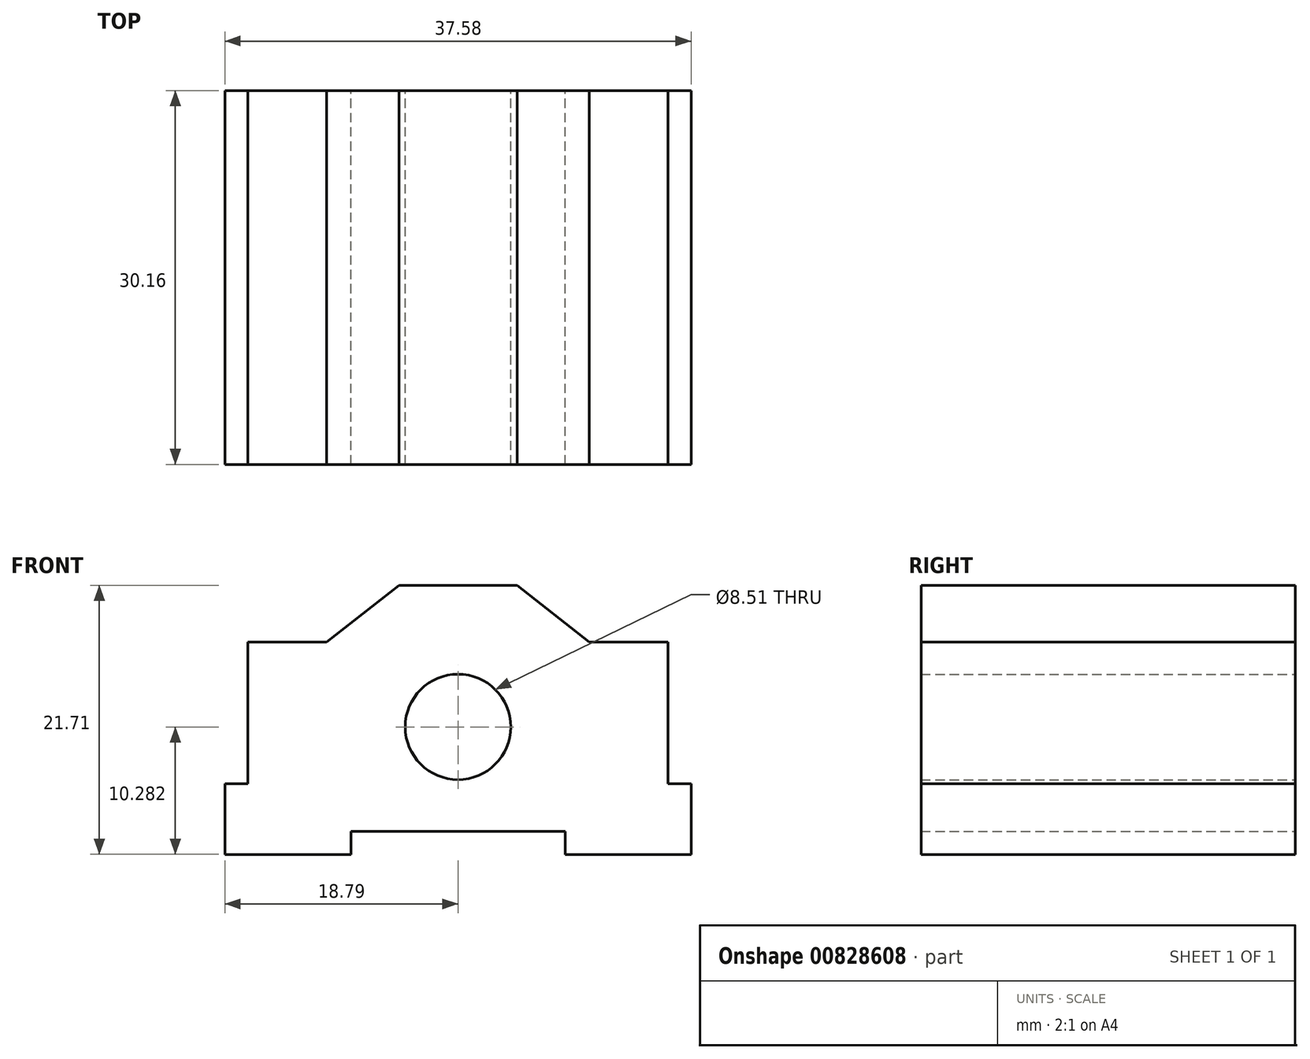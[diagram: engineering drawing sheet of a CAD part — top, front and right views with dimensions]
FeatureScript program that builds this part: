
annotation { "Feature Type Name" : "Feature", "Feature Type Description" : "" }
export const myFeature = defineFeature(function(context is Context, id is Id, definition is map)
    precondition{}
    {
        {
            var Q0;
            Q0=qCreatedBy(makeId("Front.planeOp"),FACE);
            var sketch = newSketch(context, id + "F0", { "sketchPlane" : qUnion([Q0])});
            skLineSegment(sketch, "E0", {"start": v(4.76, 4.57) * mm, "end": v(10.59, 0) * mm});
            skLineSegment(sketch, "E1", {"start": v(10.59, 0) * mm, "end": v(16.94, 0) * mm});
            skLineSegment(sketch, "E2", {"start": v(16.94, 0) * mm, "end": v(16.94, -11.43) * mm});
            skLineSegment(sketch, "E3", {"start": v(16.94, -11.43) * mm, "end": v(18.79, -11.43) * mm});
            skLineSegment(sketch, "E4", {"start": v(18.79, -11.43) * mm, "end": v(18.79, -17.15) * mm});
            skLineSegment(sketch, "E5", {"start": v(18.79, -17.14) * mm, "end": v(8.63, -17.14) * mm});
            skLineSegment(sketch, "E6", {"start": v(8.63, -17.14) * mm, "end": v(8.63, -15.3) * mm});
            skLineSegment(sketch, "E7", {"start": v(8.63, -15.3) * mm, "end": v(0, -15.3) * mm});
            skLineSegment(sketch, "E8", {"start": v(4.76, 4.57) * mm, "end": v(0, 4.57) * mm});
            skLineSegment(sketch, "E9.MirrorCS", {"start": v(-16.94, -11.43) * mm, "end": v(-18.79, -11.43) * mm});
            skLineSegment(sketch, "E10.MirrorCS", {"start": v(-8.63, -17.14) * mm, "end": v(-8.63, -15.3) * mm});
            skLineSegment(sketch, "E11.MirrorCS", {"start": v(-16.94, 0) * mm, "end": v(-16.94, -11.43) * mm});
            skLineSegment(sketch, "E12.MirrorCS", {"start": v(-10.59, 0) * mm, "end": v(-16.94, 0) * mm});
            skLineSegment(sketch, "E13.MirrorCS", {"start": v(-18.79, -11.43) * mm, "end": v(-18.79, -17.15) * mm});
            skLineSegment(sketch, "E14.MirrorCS", {"start": v(-4.76, 4.57) * mm, "end": v(-10.59, 0) * mm});
            skLineSegment(sketch, "E15.MirrorCS", {"start": v(-8.63, -15.3) * mm, "end": v(0, -15.3) * mm});
            skLineSegment(sketch, "E16.MirrorCS", {"start": v(-18.79, -17.15) * mm, "end": v(-8.63, -17.15) * mm});
            skLineSegment(sketch, "E17.MirrorCS", {"start": v(-4.76, 4.57) * mm, "end": v(0, 4.57) * mm});
            skCircle(sketch, "E18", {"center": v(0, -6.86) * mm, "radius": 4.25 * mm});
            skSolve(sketch);
        }
        {
            var Q0;
            Q0=makeQuery(id+"F0.imprint","IMPRINT",FACE,{"disambiguationData":[TD([[makeQuery(id+"F0.imprint","IMPRINT",EDGE,{"derivedFrom":sQuery(id+"F0.wireOp",EDGE,"E0")}),-1.0]])]});
            extrude(context, id + "F1", {"entities" : qUnion([Q0]), "endBound" : BoundingType.SYMMETRIC, "depth" : 30.16 * mm, "offsetDistance" : 25.4 * mm});
        }
    });
